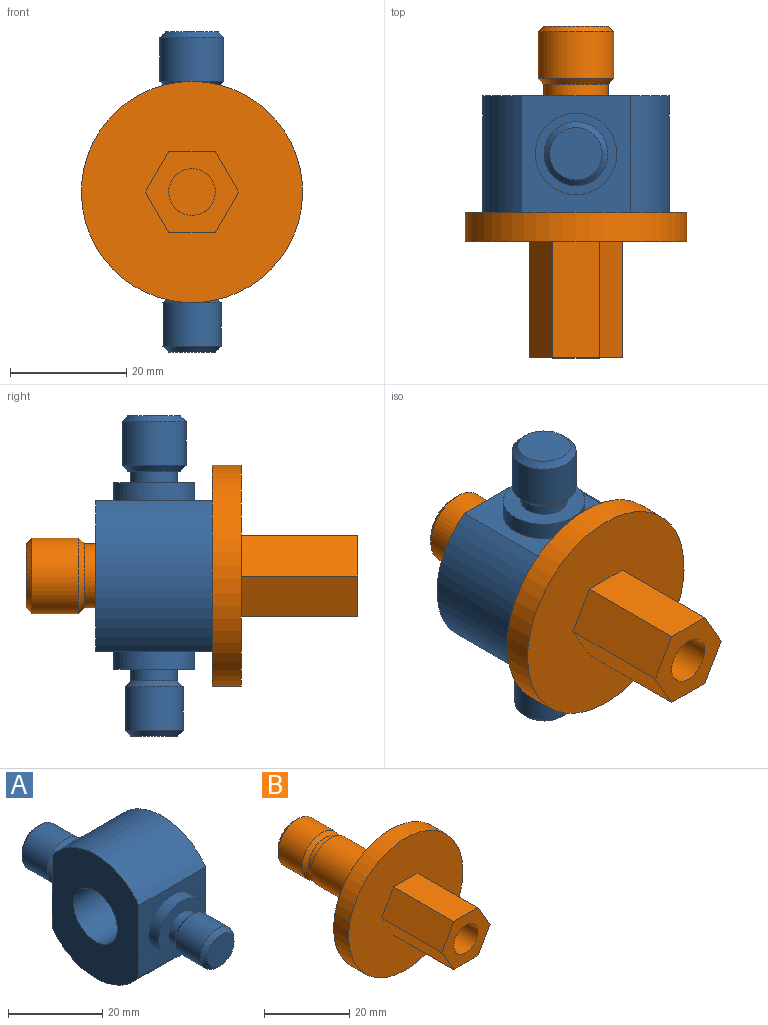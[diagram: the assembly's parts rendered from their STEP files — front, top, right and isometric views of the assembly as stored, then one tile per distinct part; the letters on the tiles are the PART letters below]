
ASSEMBLY  parts=2 mates=1
PART A: 22 faces, bbox 20x55x32 mm
  f0: plane 20x18.65mm, normal (0,1,0), area 219.2mm2, adj f1,f8,f10,f11,f12
  f1: plane 32x26mm, normal (-1,0,0), area 593.3mm2, adj f0,f2,f9,f10,f11
  f2: plane 20x18.65mm, normal (0,-1,0), area 219.2mm2, adj f1,f6,f8,f10,f11
  f3: cylinder r=5mm len=10mm, axis (0,1,0), area 235.6mm2, adj f20,f21
  f4: plane 8x8mm, normal (0,-1,0), area 50.3mm2, adj f21
  f5: cylinder r=4mm len=8mm, axis (0,-1,0), area 50.3mm2, adj f7,f20
  f6: cylinder r=7mm len=14mm, axis (0,-1,0), area 131.9mm2, adj f2,f7
  f7: plane 14x14mm, normal (0,-1,0), area 103.7mm2, adj f5,f6
  f8: plane 32x26mm, normal (1,0,0), area 593.3mm2, adj f0,f2,f9,f10,f11
  f9: cylinder r=6.55mm len=20mm, axis (1,0,0), area 823.1mm2, adj f1,f8
  f10: cylinder r=16mm len=26mm, axis (1,0,0), area 607mm2, adj f0,f1,f2,f8
  f11: cylinder r=16mm len=26mm, axis (1,0,0), area 607mm2, adj f0,f1,f2,f8
  f12: cylinder r=7mm len=14mm, axis (0,-1,0), area 131.9mm2, adj f0,f13
  f13: plane 14x14mm, normal (0,1,0), area 103.7mm2, adj f12,f14
  f14: cylinder r=4mm len=8mm, axis (0,-1,0), area 50.3mm2, adj f13,f17
  f15: cylinder r=5.5mm len=11mm, axis (0,-1,0), area 259.2mm2, adj f18,f19
  f16: plane 9x9mm, normal (0,1,0), area 63.6mm2, adj f18
  f17: plane 9x9mm, normal (0,-1,0), area 13.4mm2, adj f14,f19
  f18: cone r=4.5mm half-angle=45deg, axis (0,-1,0), area 44.4mm2, adj f15,f16
  f19: cone r=5.5mm half-angle=45deg, axis (0,1,0), area 44.4mm2, adj f15,f17
  f20: cone r=5mm half-angle=45deg, axis (0,-1,0), area 40mm2, adj f3,f5
  f21: cone r=4mm half-angle=45deg, axis (0,1,0), area 40mm2, adj f3,f4
PART B: 19 faces, bbox 38x57x38 mm
  f0: plane 20x8mm, normal (0,0,1), area 160mm2, adj f1,f5,f7,f9
  f1: plane 20x6.93mm, normal (-0.87,0,0.5), area 160mm2, adj f0,f2,f7,f9
  f2: plane 20x6.93mm, normal (-0.87,0,-0.5), area 160mm2, adj f1,f3,f7,f9
  f3: plane 20x8mm, normal (0,0,-1), area 160mm2, adj f2,f4,f7,f9
  f4: plane 20x6.93mm, normal (0.87,0,-0.5), area 160mm2, adj f3,f5,f7,f9
  f5: plane 20x6.93mm, normal (0.87,0,0.5), area 160mm2, adj f0,f4,f7,f9
  f6: cylinder r=4mm len=20mm, axis (0,1,0), area 502.7mm2, adj f7,f8
  f7: plane 16x13.86mm, normal (0,-1,0), area 116mm2, adj f0,f1,f2,f3,f4,f5,f6
  f8: plane 8x8mm, normal (0,-1,0), area 50.3mm2, adj f6
  f9: plane 38x38mm, normal (0,-1,0), area 967.8mm2, adj f0,f1,f2,f3,f4,f5,f10
  f10: cylinder r=19mm len=38mm, axis (0,-1,0), area 596.9mm2, adj f9,f11
  f11: plane 38x38mm, normal (0,1,0), area 1001.4mm2, adj f10,f12
  f12: cylinder r=6.5mm len=20mm, axis (0,-1,0), area 816.8mm2, adj f11,f13
  f13: plane 13x13mm, normal (0,1,0), area 37.7mm2, adj f12,f14
  f14: cylinder r=5.5mm len=11mm, axis (0,-1,0), area 69.1mm2, adj f13,f17
  f15: cylinder r=6.5mm len=13mm, axis (0,-1,0), area 326.7mm2, adj f17,f18
  f16: plane 11x11mm, normal (0,1,0), area 95mm2, adj f18
  f17: cone r=6.5mm half-angle=45deg, axis (0,1,0), area 53.3mm2, adj f14,f15
  f18: cone r=5.5mm half-angle=45deg, axis (0,-1,0), area 53.3mm2, adj f15,f16
PLACE A rot(axis=(0.58,-0.58,-0.58),120deg) t=(41.37,26.5,41.01)mm
PLACE B t=(-33.49,11.5,59.01)mm
MATE fastened A.f9 <-> B.f12  axis (0,-1,0) through (-33.49,26.5,59.01)mm
